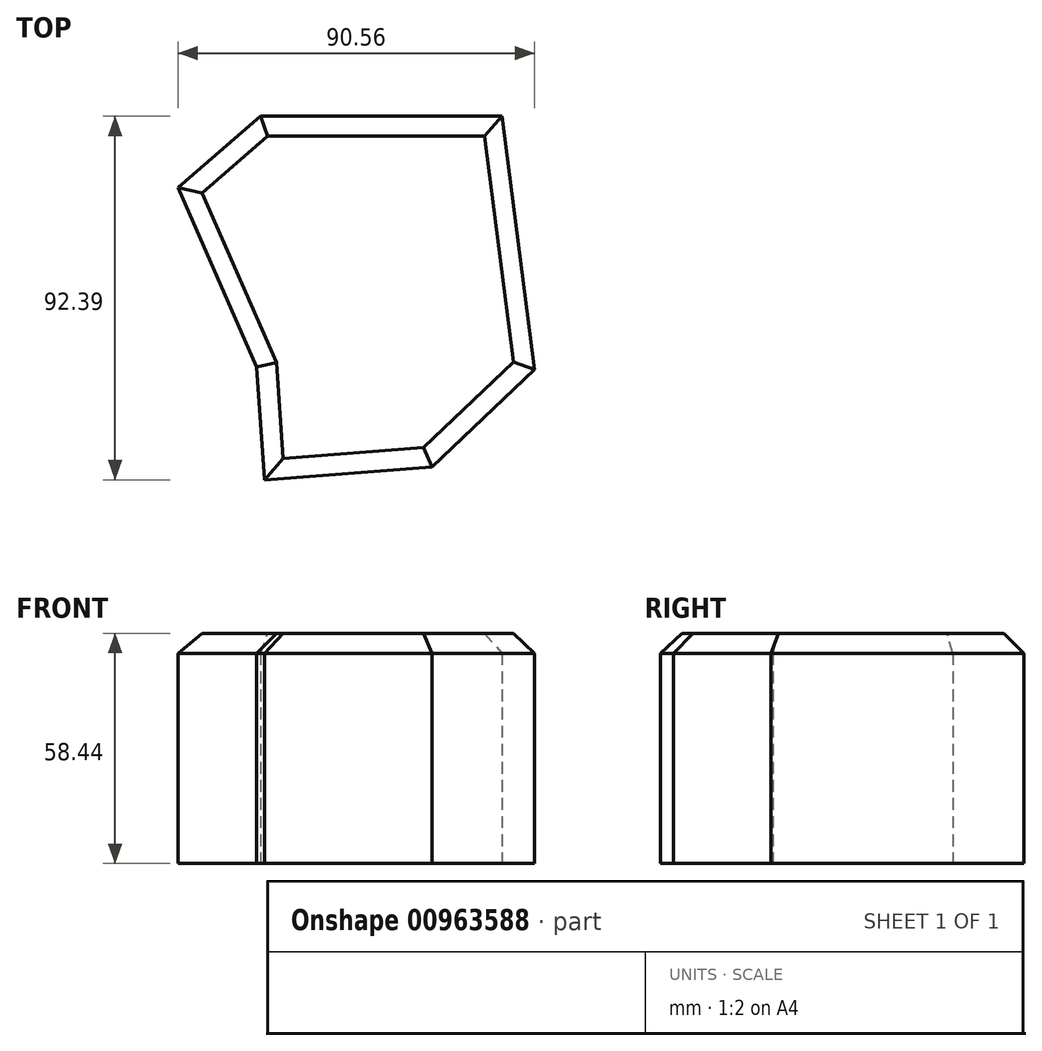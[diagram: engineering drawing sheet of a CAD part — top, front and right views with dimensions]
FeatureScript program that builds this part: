
annotation { "Feature Type Name" : "Feature", "Feature Type Description" : "" }
export const myFeature = defineFeature(function(context is Context, id is Id, definition is map)
    precondition{}
    {
        {
            var Q0;
            Q0=qCreatedBy(makeId("Top.planeOp"),FACE);
            var sketch = newSketch(context, id + "F0", { "sketchPlane" : qUnion([Q0])});
            skLineSegment(sketch, "E0", {"start": v(-39.23, 11.55) * mm, "end": v(-18.33, 29.7) * mm});
            skLineSegment(sketch, "E1", {"start": v(-18.33, 29.7) * mm, "end": v(43.08, 29.7) * mm});
            skLineSegment(sketch, "E2", {"start": v(43.08, 29.7) * mm, "end": v(51.33, -34.65) * mm});
            skLineSegment(sketch, "E3", {"start": v(51.33, -34.65) * mm, "end": v(25.3, -59.4) * mm});
            skLineSegment(sketch, "E4", {"start": v(25.3, -59.4) * mm, "end": v(-17.23, -62.7) * mm});
            skLineSegment(sketch, "E5", {"start": v(-17.23, -62.7) * mm, "end": v(-19.25, -34.1) * mm});
            skFitSpline(sketch, "E6", {"points": [v(-19.25, -34.1) * mm, v(-39.23, 11.55) * mm], "startDerivative": vector(-19.98, 45.64) * mm, "endDerivative": vector(-19.98, 45.64) * mm});
            skSolve(sketch);
        }
        {
            var Q0;
            Q0=makeQuery(id+"F0.imprint","IMPRINT",FACE,{"disambiguationData":[TD([[makeQuery(id+"F0.imprint","IMPRINT",EDGE,{"derivedFrom":sQuery(id+"F0.wireOp",EDGE,"E0")}),-1.0]])]});
            extrude(context, id + "F1", {"entities" : qUnion([Q0]), "depth" : 58.44 * mm, "offsetDistance" : 25.4 * mm});
        }
        {
            var Q0;
            Q0=makeQuery(id+"F1.opExtrude","CAP_FACE",FACE,{"disambiguationData":[OSD([sQuery(id+"F0.wireOp",EDGE,"E0"),sQuery(id+"F0.wireOp",EDGE,"E1"),sQuery(id+"F0.wireOp",EDGE,"E2"),sQuery(id+"F0.wireOp",EDGE,"E3"),sQuery(id+"F0.wireOp",EDGE,"E4"),sQuery(id+"F0.wireOp",EDGE,"E5"),sQuery(id+"F0.wireOp",EDGE,"E6")])],"isStart":false});
            chamfer(context, id + "F2", {"entities" : qUnion([Q0]), "width" : 5.08 * mm, "tangentPropagation" : true});
        }
    });
